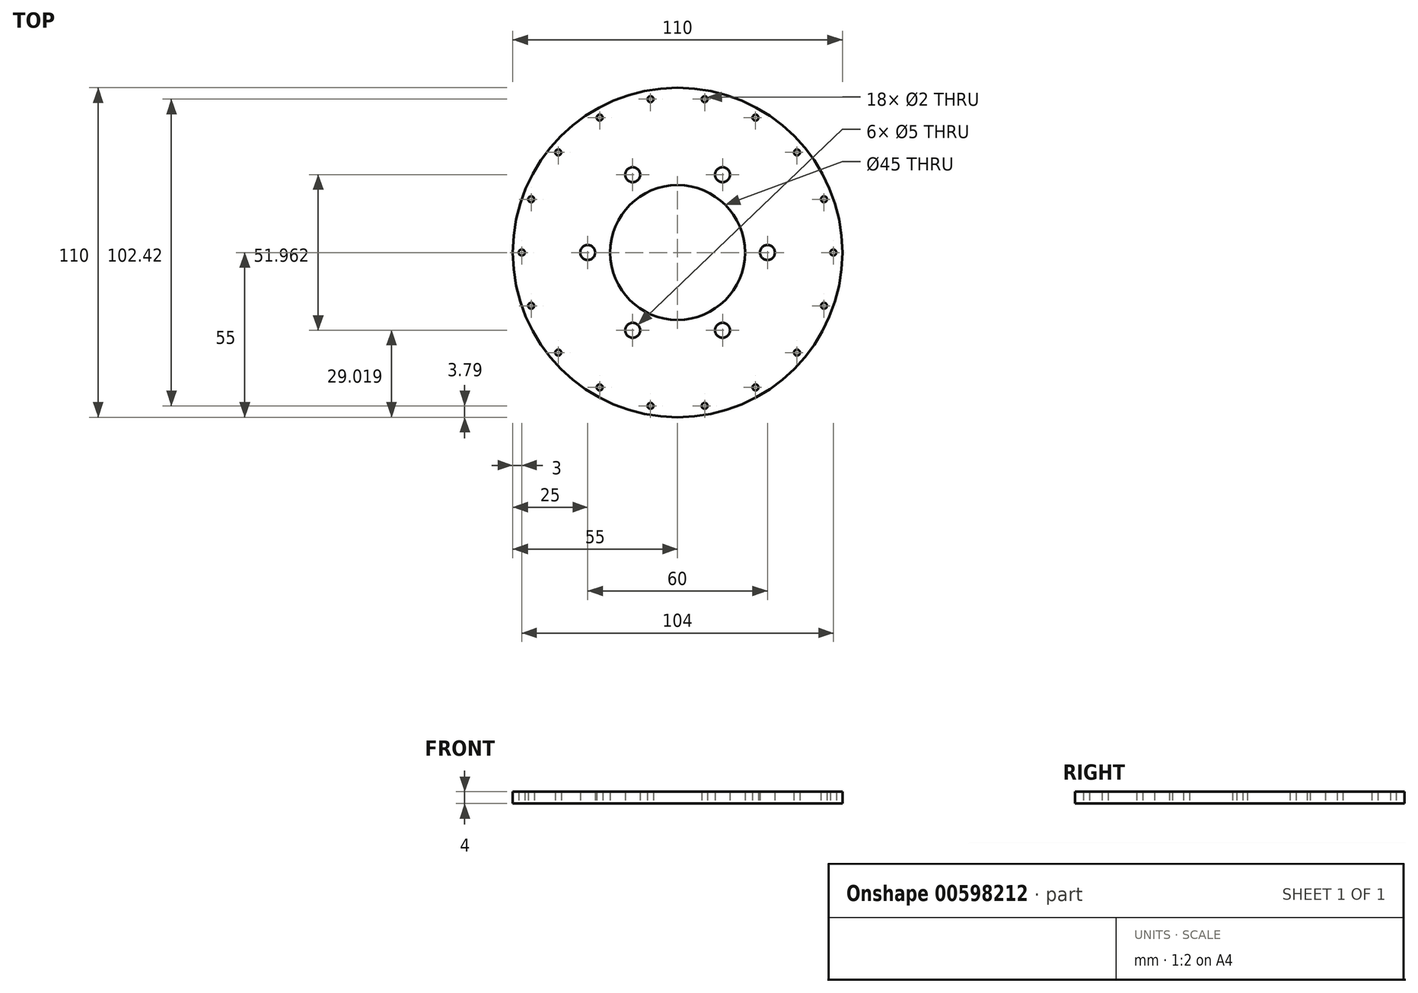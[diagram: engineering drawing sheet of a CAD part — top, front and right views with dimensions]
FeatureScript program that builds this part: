
annotation { "Feature Type Name" : "Feature", "Feature Type Description" : "" }
export const myFeature = defineFeature(function(context is Context, id is Id, definition is map)
    precondition{}
    {
        {
            var Q0;
            Q0=qCreatedBy(makeId("Top.planeOp"),FACE);
            var sketch = newSketch(context, id + "F0", { "sketchPlane" : qUnion([Q0])});
            skCircle(sketch, "E0", {"center": v(0, 0) * mm, "radius": 55 * mm});
            skCircle(sketch, "E1", {"center": v(0, 0) * mm, "radius": 22.5 * mm});
            skCircle(sketch, "E2", {"center": v(30, 0) * mm, "radius": 2.5 * mm});
            skCircle(sketch, "E3.1.0", {"center": v(15, 25.98) * mm, "radius": 2.5 * mm});
            skCircle(sketch, "E3.2.0", {"center": v(-15, 25.98) * mm, "radius": 2.5 * mm});
            skCircle(sketch, "E3.3.0", {"center": v(-30, 0) * mm, "radius": 2.5 * mm});
            skCircle(sketch, "E3.4.0", {"center": v(-15, -25.98) * mm, "radius": 2.5 * mm});
            skCircle(sketch, "E3.5.0", {"center": v(15, -25.98) * mm, "radius": 2.5 * mm});
            skLineSegment(sketch, "E4", {"start": v(0, 0) * mm, "end": v(85.98, 0) * mm});
            skCircle(sketch, "E5", {"center": v(52, 0) * mm, "radius": 1 * mm});
            skCircle(sketch, "E6", {"center": v(26, 45.03) * mm, "radius": 1 * mm});
            skCircle(sketch, "E7.1.0", {"center": v(39.83, 33.42) * mm, "radius": 1 * mm});
            skCircle(sketch, "E7.1.1", {"center": v(-9.03, 51.21) * mm, "radius": 1 * mm});
            skCircle(sketch, "E7.2.0", {"center": v(9.03, 51.21) * mm, "radius": 1 * mm});
            skCircle(sketch, "E7.2.1", {"center": v(-39.83, 33.42) * mm, "radius": 1 * mm});
            skCircle(sketch, "E7.3.0", {"center": v(-26, 45.03) * mm, "radius": 1 * mm});
            skCircle(sketch, "E7.3.1", {"center": v(-52, 0) * mm, "radius": 1 * mm});
            skCircle(sketch, "E7.4.0", {"center": v(-48.86, 17.79) * mm, "radius": 1 * mm});
            skCircle(sketch, "E7.4.1", {"center": v(-39.83, -33.42) * mm, "radius": 1 * mm});
            skCircle(sketch, "E7.5.0", {"center": v(-48.86, -17.79) * mm, "radius": 1 * mm});
            skCircle(sketch, "E7.5.1", {"center": v(-9.03, -51.21) * mm, "radius": 1 * mm});
            skCircle(sketch, "E7.6.0", {"center": v(-26, -45.03) * mm, "radius": 1 * mm});
            skCircle(sketch, "E7.6.1", {"center": v(26, -45.03) * mm, "radius": 1 * mm});
            skCircle(sketch, "E7.7.0", {"center": v(9.03, -51.21) * mm, "radius": 1 * mm});
            skCircle(sketch, "E7.7.1", {"center": v(48.86, -17.79) * mm, "radius": 1 * mm});
            skCircle(sketch, "E7.8.0", {"center": v(39.83, -33.42) * mm, "radius": 1 * mm});
            skCircle(sketch, "E7.8.1", {"center": v(48.86, 17.79) * mm, "radius": 1 * mm});
            skSolve(sketch);
        }
        {
            var Q0;
            Q0=makeQuery(id+"F0.imprint","IMPRINT",FACE,{"disambiguationData":[TD([[makeQuery(id+"F0.imprint","IMPRINT",EDGE,{"derivedFrom":sQuery(id+"F0.wireOp",EDGE,"E0")}),1.0]])]});
            extrude(context, id + "F1", {"entities" : qUnion([Q0]), "depth" : 4 * mm, "offsetDistance" : 25 * mm});
        }
    });
